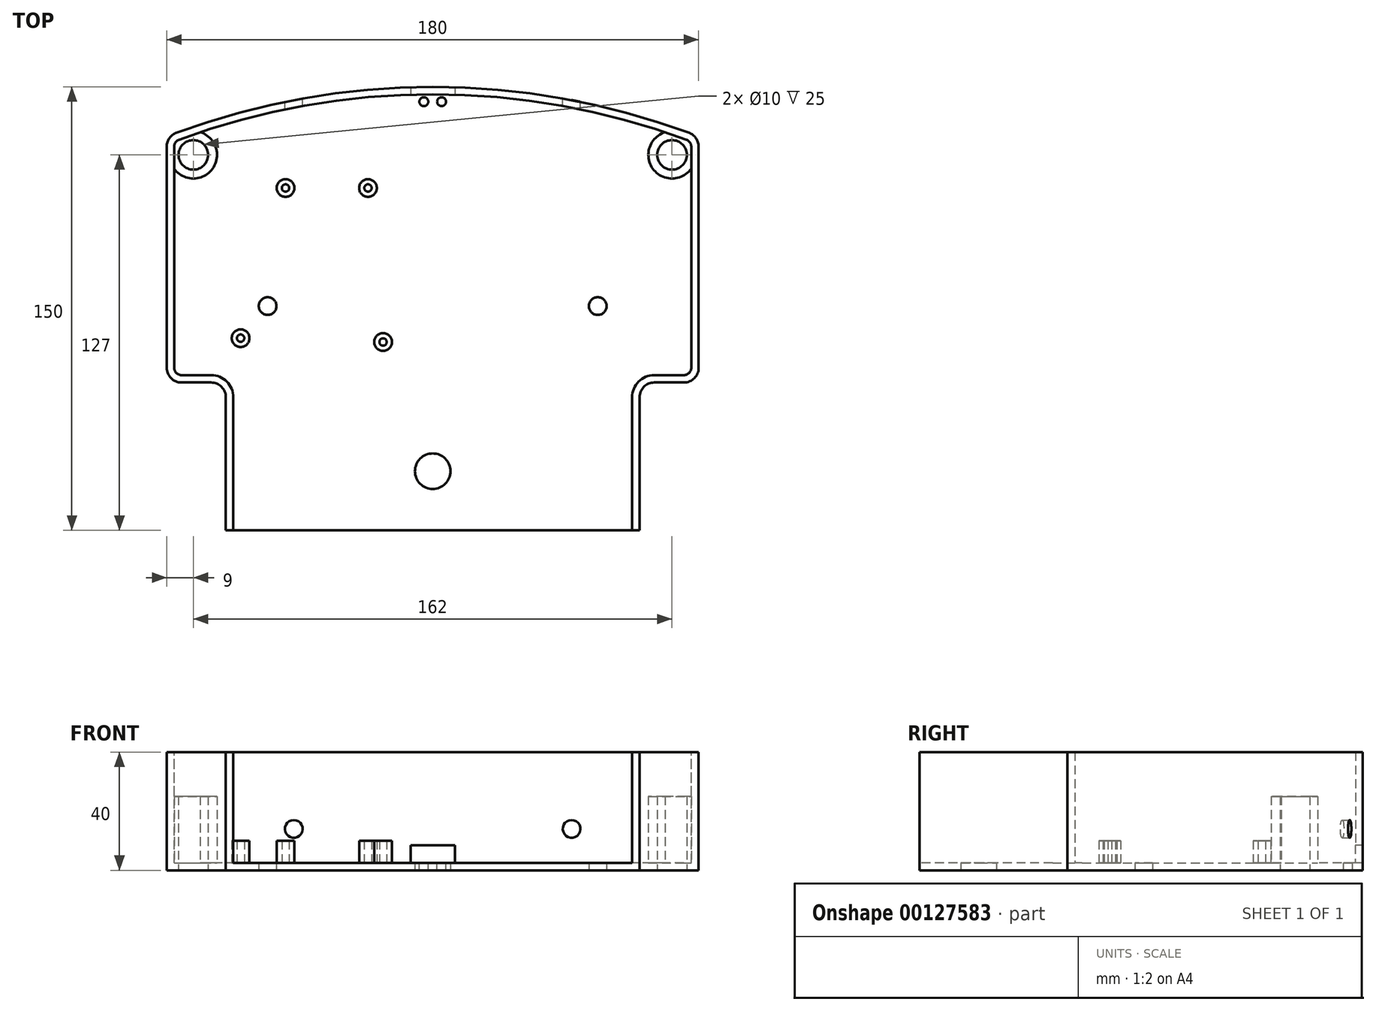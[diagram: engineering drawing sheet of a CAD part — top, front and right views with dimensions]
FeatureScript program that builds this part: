
annotation { "Feature Type Name" : "Feature", "Feature Type Description" : "" }
export const myFeature = defineFeature(function(context is Context, id is Id, definition is map)
    precondition{}
    {
        {
            var Q0;
            Q0=qCreatedBy(makeId("Top.planeOp"),FACE);
            var sketch = newSketch(context, id + "F0", { "sketchPlane" : qUnion([Q0])});
            skLineSegment(sketch, "E0.bottom", {"start": v(-90, -50) * mm, "end": v(90, -50) * mm});
            skLineSegment(sketch, "E0.top", {"start": v(-90, 100) * mm, "end": v(90, 100) * mm});
            skLineSegment(sketch, "E0.left", {"start": v(-90, -50) * mm, "end": v(-90, 100) * mm});
            skLineSegment(sketch, "E0.right", {"start": v(90, -50) * mm, "end": v(90, 100) * mm});
            skCircle(sketch, "E1", {"center": v(0, -150) * mm, "radius": 250 * mm});
            skSolve(sketch);
        }
        {
            var Q0;
            {var subQ4=sQuery(id+"F0.wireOp",EDGE,"E0.bottom");Q0=makeQuery(id+"F0.imprint","IMPRINT",FACE,{"disambiguationData":[TD([[makeQuery(id+"F0.imprint","IMPRINT",EDGE,{"derivedFrom":subQ4}),1.0]])]});}
            extrude(context, id + "F1", {"entities" : qUnion([Q0]), "depth" : 40 * mm});
        }
        {
            var Q0;
            Q0=qCreatedBy(makeId("Top.planeOp"),FACE);
            var sketch = newSketch(context, id + "F2", { "sketchPlane" : qUnion([Q0])});
            skLineSegment(sketch, "E2.bottom", {"start": v(-170, 0) * mm, "end": v(-70, 0) * mm});
            skLineSegment(sketch, "E2.top", {"start": v(-170, -200) * mm, "end": v(-70, -200) * mm});
            skLineSegment(sketch, "E2.left", {"start": v(-170, 0) * mm, "end": v(-170, -200) * mm});
            skLineSegment(sketch, "E2.right", {"start": v(-70, 0) * mm, "end": v(-70, -200) * mm});
            skLineSegment(sketch, "E3.bottom", {"start": v(170, 0) * mm, "end": v(70, 0) * mm});
            skLineSegment(sketch, "E3.top", {"start": v(170, -200) * mm, "end": v(70, -200) * mm});
            skLineSegment(sketch, "E3.left", {"start": v(170, 0) * mm, "end": v(170, -200) * mm});
            skLineSegment(sketch, "E3.right", {"start": v(70, 0) * mm, "end": v(70, -200) * mm});
            skSolve(sketch);
        }
        {
            var Q0;
            Q0=makeQuery(id+"F2.imprint","IMPRINT",FACE,{"disambiguationData":[TD([[makeQuery(id+"F2.imprint","IMPRINT",EDGE,{"derivedFrom":sQuery(id+"F2.wireOp",EDGE,"E2.bottom")}),-1.0]])]});
            var Q1;
            Q1=makeQuery(id+"F2.imprint","IMPRINT",FACE,{"disambiguationData":[TD([[makeQuery(id+"F2.imprint","IMPRINT",EDGE,{"derivedFrom":sQuery(id+"F2.wireOp",EDGE,"E3.bottom")}),1.0]])]});
            extrude(context, id + "F3", {"entities" : qUnion([Q0, Q1]), "operationType" : NewBodyOperationType.REMOVE, "depth" : 100 * mm});
        }
        {
            var Q0;
            Q0=makeQuery(id+"F1.opExtrude","SWEPT_EDGE",EDGE,{"disambiguationData":[OSD([sQuery(id+"F0.wireOp",EDGE,"E0.left"),sQuery(id+"F0.wireOp",EDGE,"E1")])]});
            var Q1;
            Q1=makeQuery(id+"F1.opExtrude","SWEPT_EDGE",EDGE,{"disambiguationData":[OSD([sQuery(id+"F0.wireOp",EDGE,"E0.right"),sQuery(id+"F0.wireOp",EDGE,"E1")])]});
            var Q2;
            Q2=makeQuery(id+"F3.boolean.opBoolean","INTERSECT",EDGE,{"derivedFrom":[makeQuery(id+"F1.opExtrude","SWEPT_FACE",FACE,{"disambiguationData":[OSD([sQuery(id+"F0.wireOp",EDGE,"E0.right")])]}),makeQuery(id+"F3.opExtrude","SWEPT_FACE",FACE,{"disambiguationData":[OSD([sQuery(id+"F2.wireOp",EDGE,"E3.bottom")])]})]});
            var Q3;
            Q3=makeQuery(id+"F3.boolean.opBoolean","COPY",EDGE,{"derivedFrom":makeQuery(id+"F3.opExtrude","SWEPT_EDGE",EDGE,{"disambiguationData":[OSD([sQuery(id+"F2.wireOp",EDGE,"E3.bottom"),sQuery(id+"F2.wireOp",EDGE,"E3.right")])]})});
            var Q4;
            Q4=makeQuery(id+"F3.boolean.opBoolean","INTERSECT",EDGE,{"derivedFrom":[makeQuery(id+"F1.opExtrude","SWEPT_FACE",FACE,{"disambiguationData":[OSD([sQuery(id+"F0.wireOp",EDGE,"E0.left")])]}),makeQuery(id+"F3.opExtrude","SWEPT_FACE",FACE,{"disambiguationData":[OSD([sQuery(id+"F2.wireOp",EDGE,"E2.bottom")])]})]});
            var Q5;
            Q5=makeQuery(id+"F3.boolean.opBoolean","COPY",EDGE,{"derivedFrom":makeQuery(id+"F3.opExtrude","SWEPT_EDGE",EDGE,{"disambiguationData":[OSD([sQuery(id+"F2.wireOp",EDGE,"E2.bottom"),sQuery(id+"F2.wireOp",EDGE,"E2.right")])]})});
            fillet(context, id + "F4", {"entities" : qUnion([Q0, Q1, Q2, Q3, Q4, Q5]), "radius" : 5 * mm, "tangentPropagation" : true, "allowEdgeOverflow" : false});
        }
        {
            var Q0;
            Q0=makeQuery(id+"F1.opExtrude","CAP_FACE",FACE,{"disambiguationData":[OSD([sQuery(id+"F0.wireOp",EDGE,"E0.bottom"),sQuery(id+"F0.wireOp",EDGE,"E0.left"),sQuery(id+"F0.wireOp",EDGE,"E0.right"),sQuery(id+"F0.wireOp",EDGE,"E1")])],"isStart":false});
            var Q1;
            Q1=makeQuery(id+"F1.opExtrude","SWEPT_FACE",FACE,{"disambiguationData":[OSD([sQuery(id+"F0.wireOp",EDGE,"E0.bottom")])]});
            shell(context, id + "F5", {"entities" : qUnion([Q0, Q1]), "thickness" : 2.5 * mm});
        }
        {
            var Q0;
            Q0=qCreatedBy(makeId("Top.planeOp"),FACE);
            var sketch = newSketch(context, id + "F6", { "sketchPlane" : qUnion([Q0])});
            skCircle(sketch, "E4", {"center": v(0, -30) * mm, "radius": 6 * mm});
            skSolve(sketch);
        }
        {
            var Q0;
            Q0=makeQuery(id+"F6.imprint","IMPRINT",FACE,{"disambiguationData":[TD([[makeQuery(id+"F6.imprint","IMPRINT",EDGE,{"derivedFrom":sQuery(id+"F6.wireOp",EDGE,"E4")}),1.0]])]});
            extrude(context, id + "F7", {"entities" : qUnion([Q0]), "operationType" : NewBodyOperationType.REMOVE, "depth" : 25 * mm});
        }
        {
            var Q0;
            Q0=qCreatedBy(makeId("Top.planeOp"),FACE);
            var sketch = newSketch(context, id + "F8", { "sketchPlane" : qUnion([Q0])});
            skCircle(sketch, "E5", {"center": v(-55.86, 25.86) * mm, "radius": 3 * mm});
            skCircle(sketch, "E6", {"center": v(55.86, 25.86) * mm, "radius": 3 * mm});
            skLineSegment(sketch, "E7", {"start": v(0, -30) * mm, "end": v(-55.86, 25.86) * mm, "construction": true});
            skLineSegment(sketch, "E8", {"start": v(0, -30) * mm, "end": v(55.86, 25.86) * mm, "construction": true});
            skSolve(sketch);
        }
        {
            var Q0;
            Q0=qSketchRegion(id+"F8",true);
            extrude(context, id + "F9", {"entities" : qUnion([Q0]), "operationType" : NewBodyOperationType.REMOVE, "depth" : 25 * mm});
        }
        {
            var Q0;
            Q0=qCreatedBy(makeId("Top.planeOp"),FACE);
            var sketch = newSketch(context, id + "F10", { "sketchPlane" : qUnion([Q0])});
            skCircle(sketch, "E9", {"center": v(-81, 77) * mm, "radius": 8 * mm});
            skCircle(sketch, "E10", {"center": v(81, 77) * mm, "radius": 8 * mm});
            skSolve(sketch);
        }
        {
            var Q0;
            Q0=qSketchRegion(id+"F10",true);
            extrude(context, id + "F11", {"entities" : qUnion([Q0]), "operationType" : NewBodyOperationType.ADD, "depth" : 25 * mm});
        }
        {
            var Q0;
            Q0=qCreatedBy(makeId("Top.planeOp"),FACE);
            var sketch = newSketch(context, id + "F12", { "sketchPlane" : qUnion([Q0])});
            skCircle(sketch, "E11", {"center": v(-81, 77) * mm, "radius": 5 * mm});
            skCircle(sketch, "E12", {"center": v(81, 77) * mm, "radius": 5 * mm});
            skSolve(sketch);
        }
        {
            var Q0;
            Q0=qSketchRegion(id+"F12",true);
            extrude(context, id + "F13", {"entities" : qUnion([Q0]), "operationType" : NewBodyOperationType.REMOVE, "depth" : 25 * mm});
        }
        {
            var Q0;
            Q0=qCreatedBy(makeId("Top.planeOp"),FACE);
            var sketch = newSketch(context, id + "F14", { "sketchPlane" : qUnion([Q0])});
            skCircle(sketch, "E13", {"center": v(-65, 15) * mm, "radius": 3 * mm});
            skCircle(sketch, "E14", {"center": v(-65, 15) * mm, "radius": 1.25 * mm});
            skCircle(sketch, "E15", {"center": v(-49.8, 65.8) * mm, "radius": 1.25 * mm});
            skCircle(sketch, "E16", {"center": v(-49.8, 65.8) * mm, "radius": 3 * mm});
            skCircle(sketch, "E17", {"center": v(-21.9, 65.8) * mm, "radius": 1.25 * mm});
            skCircle(sketch, "E18", {"center": v(-21.9, 65.8) * mm, "radius": 3 * mm});
            skCircle(sketch, "E19", {"center": v(-16.8, 13.7) * mm, "radius": 1.25 * mm});
            skCircle(sketch, "E20", {"center": v(-16.8, 13.7) * mm, "radius": 3 * mm});
            skSolve(sketch);
        }
        {
            var Q0;
            Q0=qSketchRegion(id+"F14",true);
            extrude(context, id + "F15", {"entities" : qUnion([Q0]), "operationType" : NewBodyOperationType.ADD, "depth" : 10 * mm});
        }
        {
            var Q0;
            Q0=qCreatedBy(makeId("Front.planeOp"),FACE);
            var sketch = newSketch(context, id + "F16", { "sketchPlane" : qUnion([Q0])});
            skCircle(sketch, "E21", {"center": v(47, 14) * mm, "radius": 3 * mm});
            skCircle(sketch, "E22", {"center": v(-47, 14) * mm, "radius": 3 * mm});
            skSolve(sketch);
        }
        {
            var Q0;
            Q0=qSketchRegion(id+"F16",true);
            extrude(context, id + "F17", {"entities" : qUnion([Q0]), "operationType" : NewBodyOperationType.REMOVE, "endBound" : BoundingType.SYMMETRIC, "depth" : 300 * mm});
        }
        {
            var Q0;
            Q0=qCreatedBy(makeId("Front.planeOp"),FACE);
            var sketch = newSketch(context, id + "F18", { "sketchPlane" : qUnion([Q0])});
            skLineSegment(sketch, "E23.bottom", {"start": v(7.5, 8.5) * mm, "end": v(-7.5, 8.5) * mm});
            skLineSegment(sketch, "E23.top", {"start": v(7.5, 2.5) * mm, "end": v(-7.5, 2.5) * mm});
            skLineSegment(sketch, "E23.left", {"start": v(7.5, 8.5) * mm, "end": v(7.5, 2.5) * mm});
            skLineSegment(sketch, "E23.right", {"start": v(-7.5, 8.5) * mm, "end": v(-7.5, 2.5) * mm});
            skSolve(sketch);
        }
        {
            var Q0;
            Q0=makeQuery(id+"F18.imprint","IMPRINT",FACE,{"disambiguationData":[TD([[makeQuery(id+"F18.imprint","IMPRINT",EDGE,{"derivedFrom":sQuery(id+"F18.wireOp",EDGE,"E23.bottom")}),1.0]])]});
            extrude(context, id + "F19", {"entities" : qUnion([Q0]), "operationType" : NewBodyOperationType.REMOVE, "oppositeDirection" : true, "depth" : 250 * mm});
        }
        {
            var Q0;
            Q0=qCreatedBy(makeId("Top.planeOp"),FACE);
            var sketch = newSketch(context, id + "F20", { "sketchPlane" : qUnion([Q0])});
            skCircle(sketch, "E24", {"center": v(3, 95) * mm, "radius": 1.5 * mm});
            skCircle(sketch, "E25", {"center": v(-3, 95) * mm, "radius": 1.5 * mm});
            skSolve(sketch);
        }
        {
            var Q0;
            Q0=makeQuery(id+"F20.imprint","IMPRINT",FACE,{"disambiguationData":[TD([[makeQuery(id+"F20.imprint","IMPRINT",EDGE,{"derivedFrom":sQuery(id+"F20.wireOp",EDGE,"E25")}),1.0]])]});
            var Q1;
            Q1=makeQuery(id+"F20.imprint","IMPRINT",FACE,{"disambiguationData":[TD([[makeQuery(id+"F20.imprint","IMPRINT",EDGE,{"derivedFrom":sQuery(id+"F20.wireOp",EDGE,"E24")}),1.0]])]});
            extrude(context, id + "F21", {"entities" : qUnion([Q0, Q1]), "operationType" : NewBodyOperationType.REMOVE, "endBound" : BoundingType.SYMMETRIC, "oppositeDirection" : true, "depth" : 25 * mm});
        }
    });
